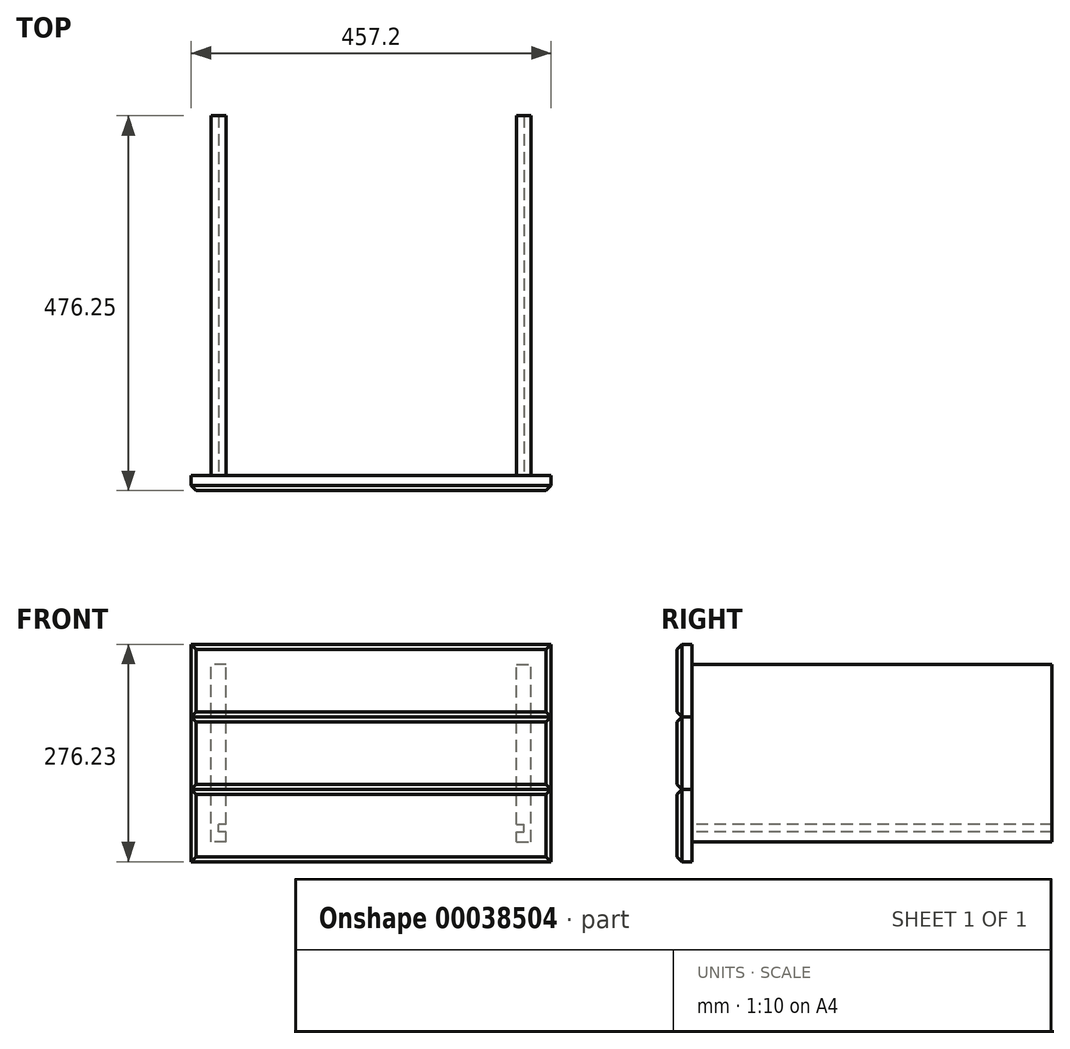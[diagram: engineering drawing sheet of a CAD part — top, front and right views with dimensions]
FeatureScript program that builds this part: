
annotation { "Feature Type Name" : "Feature", "Feature Type Description" : "" }
export const myFeature = defineFeature(function(context is Context, id is Id, definition is map)
    precondition{}
    {
        {
            var Q0;
            Q0=qCreatedBy(makeId("Front.planeOp"),FACE);
            var sketch = newSketch(context, id + "F0", { "sketchPlane" : qUnion([Q0])});
            skLineSegment(sketch, "E0.bottom", {"start": v(0, 0) * mm, "end": v(457.2, 0) * mm});
            skLineSegment(sketch, "E0.top", {"start": v(0, 92.08) * mm, "end": v(457.2, 92.08) * mm});
            skLineSegment(sketch, "E0.left", {"start": v(0, 0) * mm, "end": v(0, 92.08) * mm});
            skLineSegment(sketch, "E0.right", {"start": v(457.2, 0) * mm, "end": v(457.2, 92.08) * mm});
            skSolve(sketch);
        }
        {
            var Q0;
            Q0 = qSketchRegion(id + "F0", true);
            var Q1;
            Q1=makeQuery(id+"F0.imprint","IMPRINT",FACE,{"disambiguationData":[TD([[makeQuery(id+"F0.imprint","IMPRINT",EDGE,{"derivedFrom":sQuery(id+"F0.wireOp",EDGE,"E0.bottom")}),1.0]])]});
            extrude(context, id + "F1", {"entities" : qUnion([Q0, Q1]), "depth" : 19.05 * mm});
        }
        {
            var Q0;
            Q0=makeQuery(id+"F1.opExtrude","CAP_FACE",FACE,{"disambiguationData":[OSD([sQuery(id+"F0.wireOp",EDGE,"E0.bottom"),sQuery(id+"F0.wireOp",EDGE,"E0.top"),sQuery(id+"F0.wireOp",EDGE,"E0.left"),sQuery(id+"F0.wireOp",EDGE,"E0.right")])],"isStart":false});
            var sketch = newSketch(context, id + "F2", { "sketchPlane" : qUnion([Q0])});
            skLineSegment(sketch, "E1.bottom", {"start": v(0, 92.08) * mm, "end": v(457.2, 92.08) * mm});
            skLineSegment(sketch, "E1.top", {"start": v(0, 184.15) * mm, "end": v(457.2, 184.15) * mm});
            skLineSegment(sketch, "E1.left", {"start": v(0, 92.08) * mm, "end": v(0, 184.15) * mm});
            skLineSegment(sketch, "E1.right", {"start": v(457.2, 92.08) * mm, "end": v(457.2, 184.15) * mm});
            skSolve(sketch);
        }
        {
            var Q0;
            Q0=makeQuery(id+"F2.imprint","IMPRINT",FACE,{"disambiguationData":[TD([[makeQuery(id+"F2.imprint","IMPRINT",EDGE,{"derivedFrom":sQuery(id+"F2.wireOp",EDGE,"E1.bottom")}),1.0]])]});
            extrude(context, id + "F3", {"entities" : qUnion([Q0]), "oppositeDirection" : true, "depth" : 19.05 * mm});
        }
        {
            var Q0;
            Q0=makeQuery(id+"F3.opExtrude","CAP_FACE",FACE,{"disambiguationData":[OSD([sQuery(id+"F2.wireOp",EDGE,"E1.bottom"),sQuery(id+"F2.wireOp",EDGE,"E1.top"),sQuery(id+"F2.wireOp",EDGE,"E1.left"),sQuery(id+"F2.wireOp",EDGE,"E1.right")])],"isStart":true});
            var sketch = newSketch(context, id + "F4", { "sketchPlane" : qUnion([Q0])});
            skLineSegment(sketch, "E2.bottom", {"start": v(0, 184.15) * mm, "end": v(457.2, 184.15) * mm});
            skLineSegment(sketch, "E2.top", {"start": v(0, 276.23) * mm, "end": v(457.2, 276.23) * mm});
            skLineSegment(sketch, "E2.left", {"start": v(0, 184.15) * mm, "end": v(0, 276.23) * mm});
            skLineSegment(sketch, "E2.right", {"start": v(457.2, 184.15) * mm, "end": v(457.2, 276.23) * mm});
            skSolve(sketch);
        }
        {
            var Q0;
            Q0=makeQuery(id+"F4.imprint","IMPRINT",FACE,{"disambiguationData":[TD([[makeQuery(id+"F4.imprint","IMPRINT",EDGE,{"derivedFrom":sQuery(id+"F4.wireOp",EDGE,"E2.bottom")}),1.0]])]});
            extrude(context, id + "F5", {"entities" : qUnion([Q0]), "oppositeDirection" : true, "depth" : 19.05 * mm});
        }
        {
            var Q0;
            Q0=makeQuery(id+"F1.opExtrude","CAP_EDGE",EDGE,{"disambiguationData":[OSD([sQuery(id+"F0.wireOp",EDGE,"E0.top")])],"isStart":false});
            var Q1;
            Q1=makeQuery(id+"F1.opExtrude","CAP_EDGE",EDGE,{"disambiguationData":[OSD([sQuery(id+"F0.wireOp",EDGE,"E0.bottom")])],"isStart":false});
            var Q2;
            Q2=makeQuery(id+"F1.opExtrude","CAP_EDGE",EDGE,{"disambiguationData":[OSD([sQuery(id+"F0.wireOp",EDGE,"E0.right")])],"isStart":false});
            var Q3;
            Q3=makeQuery(id+"F1.opExtrude","CAP_EDGE",EDGE,{"disambiguationData":[OSD([sQuery(id+"F0.wireOp",EDGE,"E0.left")])],"isStart":false});
            chamfer(context, id + "F6", {"entities" : qUnion([Q0, Q1, Q2, Q3]), "width" : 6.35 * mm, "tangentPropagation" : true});
        }
        {
            var Q0;
            Q0=makeQuery(id+"F3.opExtrude","CAP_EDGE",EDGE,{"disambiguationData":[OSD([sQuery(id+"F2.wireOp",EDGE,"E1.bottom")])],"isStart":true});
            var Q1;
            Q1=makeQuery(id+"F3.opExtrude","CAP_EDGE",EDGE,{"disambiguationData":[OSD([sQuery(id+"F2.wireOp",EDGE,"E1.top")])],"isStart":true});
            var Q2;
            Q2=makeQuery(id+"F3.opExtrude","CAP_EDGE",EDGE,{"disambiguationData":[OSD([sQuery(id+"F2.wireOp",EDGE,"E1.right")])],"isStart":true});
            var Q3;
            Q3=makeQuery(id+"F3.opExtrude","CAP_EDGE",EDGE,{"disambiguationData":[OSD([sQuery(id+"F2.wireOp",EDGE,"E1.left")])],"isStart":true});
            chamfer(context, id + "F7", {"entities" : qUnion([Q0, Q1, Q2, Q3]), "width" : 6.35 * mm, "tangentPropagation" : true});
        }
        {
            var Q0;
            Q0=makeQuery(id+"F5.opExtrude","CAP_EDGE",EDGE,{"disambiguationData":[OSD([sQuery(id+"F4.wireOp",EDGE,"E2.bottom")])],"isStart":true});
            var Q1;
            Q1=makeQuery(id+"F5.opExtrude","CAP_EDGE",EDGE,{"disambiguationData":[OSD([sQuery(id+"F4.wireOp",EDGE,"E2.left")])],"isStart":true});
            var Q2;
            Q2=makeQuery(id+"F5.opExtrude","CAP_EDGE",EDGE,{"disambiguationData":[OSD([sQuery(id+"F4.wireOp",EDGE,"E2.top")])],"isStart":true});
            var Q3;
            Q3=makeQuery(id+"F5.opExtrude","CAP_EDGE",EDGE,{"disambiguationData":[OSD([sQuery(id+"F4.wireOp",EDGE,"E2.right")])],"isStart":true});
            chamfer(context, id + "F8", {"entities" : qUnion([Q0, Q1, Q2, Q3]), "width" : 6.35 * mm, "tangentPropagation" : true});
        }
        {
            var Q0;
            Q0=makeQuery(id+"F3.opExtrude","CAP_FACE",FACE,{"disambiguationData":[OSD([sQuery(id+"F2.wireOp",EDGE,"E1.bottom"),sQuery(id+"F2.wireOp",EDGE,"E1.top"),sQuery(id+"F2.wireOp",EDGE,"E1.left"),sQuery(id+"F2.wireOp",EDGE,"E1.right")])],"isStart":false});
            var sketch = newSketch(context, id + "F9", { "sketchPlane" : qUnion([Q0])});
            skLineSegment(sketch, "E3.left", {"start": v(-431.8, 25.4) * mm, "end": v(-431.8, 250.83) * mm});
            skLineSegment(sketch, "E4.left", {"start": v(-25.4, 25.4) * mm, "end": v(-25.4, 250.83) * mm});
            skLineSegment(sketch, "E4.right", {"start": v(-44.45, 25.4) * mm, "end": v(-44.45, 38.1) * mm});
            skPoint(sketch, "E5.start.orphan", {"position": v(-457.2, 0) * mm});
            skLineSegment(sketch, "E6", {"start": v(-413.19, 25.4) * mm, "end": v(-431.8, 25.4) * mm});
            skLineSegment(sketch, "E7", {"start": v(-44.45, 25.4) * mm, "end": v(-25.4, 25.4) * mm});
            skPoint(sketch, "E8.orphan", {"position": v(-413.19, 0) * mm});
            skPoint(sketch, "E9.orphan", {"position": v(-44.45, 0) * mm});
            skLineSegment(sketch, "E10", {"start": v(-413.19, 250.83) * mm, "end": v(-431.8, 250.83) * mm});
            skLineSegment(sketch, "E11", {"start": v(-44.45, 250.83) * mm, "end": v(-25.4, 250.83) * mm});
            skPoint(sketch, "E4.top.end.orphan", {"position": v(-44.45, 276.23) * mm});
            skPoint(sketch, "E3.top.end.orphan", {"position": v(-413.19, 276.23) * mm});
            skLineSegment(sketch, "E12", {"start": v(-413.19, 25.4) * mm, "end": v(-413.19, 38.1) * mm});
            skLineSegment(sketch, "E13.bottom", {"start": v(-413.19, 38.1) * mm, "end": v(-422.71, 38.1) * mm});
            skLineSegment(sketch, "E13.top", {"start": v(-413.19, 47.63) * mm, "end": v(-422.71, 47.63) * mm});
            skLineSegment(sketch, "E13.right", {"start": v(-422.71, 38.1) * mm, "end": v(-422.71, 47.63) * mm});
            skLineSegment(sketch, "E14.trimOffspring", {"start": v(-413.19, 47.62) * mm, "end": v(-413.19, 250.83) * mm});
            skLineSegment(sketch, "E15.bottom", {"start": v(-44.45, 38.1) * mm, "end": v(-34.93, 38.1) * mm});
            skLineSegment(sketch, "E15.top", {"start": v(-44.45, 47.63) * mm, "end": v(-34.93, 47.63) * mm});
            skLineSegment(sketch, "E15.right", {"start": v(-34.93, 38.1) * mm, "end": v(-34.93, 47.63) * mm});
            skLineSegment(sketch, "E16.trimOffspring", {"start": v(-44.45, 47.63) * mm, "end": v(-44.45, 250.83) * mm});
            skSolve(sketch);
        }
        {
            var Q0;
            Q0 = qSketchRegion(id + "F9", true);
            extrude(context, id + "F10", {"entities" : qUnion([Q0]), "depth" : 457.2 * mm});
        }
    });
